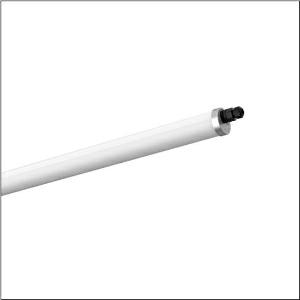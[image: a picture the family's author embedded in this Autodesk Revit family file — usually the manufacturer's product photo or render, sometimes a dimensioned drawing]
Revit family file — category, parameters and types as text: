
# Revit family: monsun_r__31_tube_51ft10dn480a_9fe9
name_source: partatom
category: Lighting Fixtures
units: mm (PartAtom-declared; Revit-internal decimal feet)

## family parameters
Cut with Voids When Loaded = No
Host = Face
Light Source = No
Part Type = Normal
Room Calculation Point = No
Round Connector Dimension = Use Diameter
Shared = No

## types (1)
- Monsun® 31 Tube (1 x LED, 8000 lm, 50 W, 4000K)
    Apparent Load = 50 VA
    CIE Flux Codes = 42 71 89 91 100
    Color Rendering = 80
    Color Temperature = 4000K
    Default Elevation = 1800 mm
    Description = Monsun® 31 Tube, tubular luminaire, primary optical cover: diffuser, of PMMA, light emission: direct distribution, primary light characteristic: symmetric, installation type: suspended mounting, surface-mounted, LED, rated luminous flux: 8.000lm, luminous efficacy: 160lm/W, light colour: 840, colour temperature: 4000K, with with 1 terminal, 5-pole, max. 2.5mm², through-wiring: 5x 1.5mm², mains connection: 220..240V, AC, 50/60Hz, rated input power: 50W, housing, cylindrical, of PMMA, semi-transparent, matt white, with luminaire and ceiling fastening, V4A, mounting with brackets of stainless steel, length: 1.570mm, diameter: 75mm, end cap, of stainless steel (V4A), protection rating (complete): IP67/IP69K, insulation class (complete): insulation class I (protective earthing), certification: CE, UKCA, impact resistance: IK07, permissible operating ambient temperature: -20..+40°C, corresponds to IFS (International Featured Standards) requirements for safety and quality in the food industry, usage in unprotected outdoor area possible with horizontal mounting, contact your sales advisor before using the luminaires in applications with unclear chemical exposure, large temperature fluctuations or condensation-forming humidity, packaging unit: 1 piece
    Height = 83 mm
    Lamp = 1 x LED
    Lamp Light Flux = 8000 lm
    Lamp Power = 50 W
    Lamp count = 1
    Length = 1570 mm
    Luminous efficacy = 160 lm/W
    Manufacturer = Siteco
    ModVariant = No
    Model = 51FT10DN480A
    Mounting Place = Ceiling
    Mounting Type = Pendant
    Number of Poles = 1
    OnlyDefault = Yes
    Power Factor = 1
    Product Name = Monsun® 31 Tube
    Product group = tubular luminaire
    ProductGroupID = 906
    Protection Class = Protection class I
    RLX_Detail_Level = 1
    RLX_Emergency_Light_Flux = 0 lm
    RLX_Emergency_Type = 0
    RLX_Emergency_Type_DB = No
    RlxData = <blob elided: 25385 chars, md5=3368d364>
    Socket = socket
    Standby Power = 0 W
    System Light Flux = 8000 lm
    System Power = 50 W
    Type Comments = Product without accessories
    Type Image = l_1228461.jpg
    URL = http://relux.com
    VarID = ---
    Voltage = 0 V
    Weight = 0.00 kg
    Width = 75 mm

## geometry (parser evidence)
native form markers: Blend x4, Sweep x14
no freeform markers — native parametric forms only
